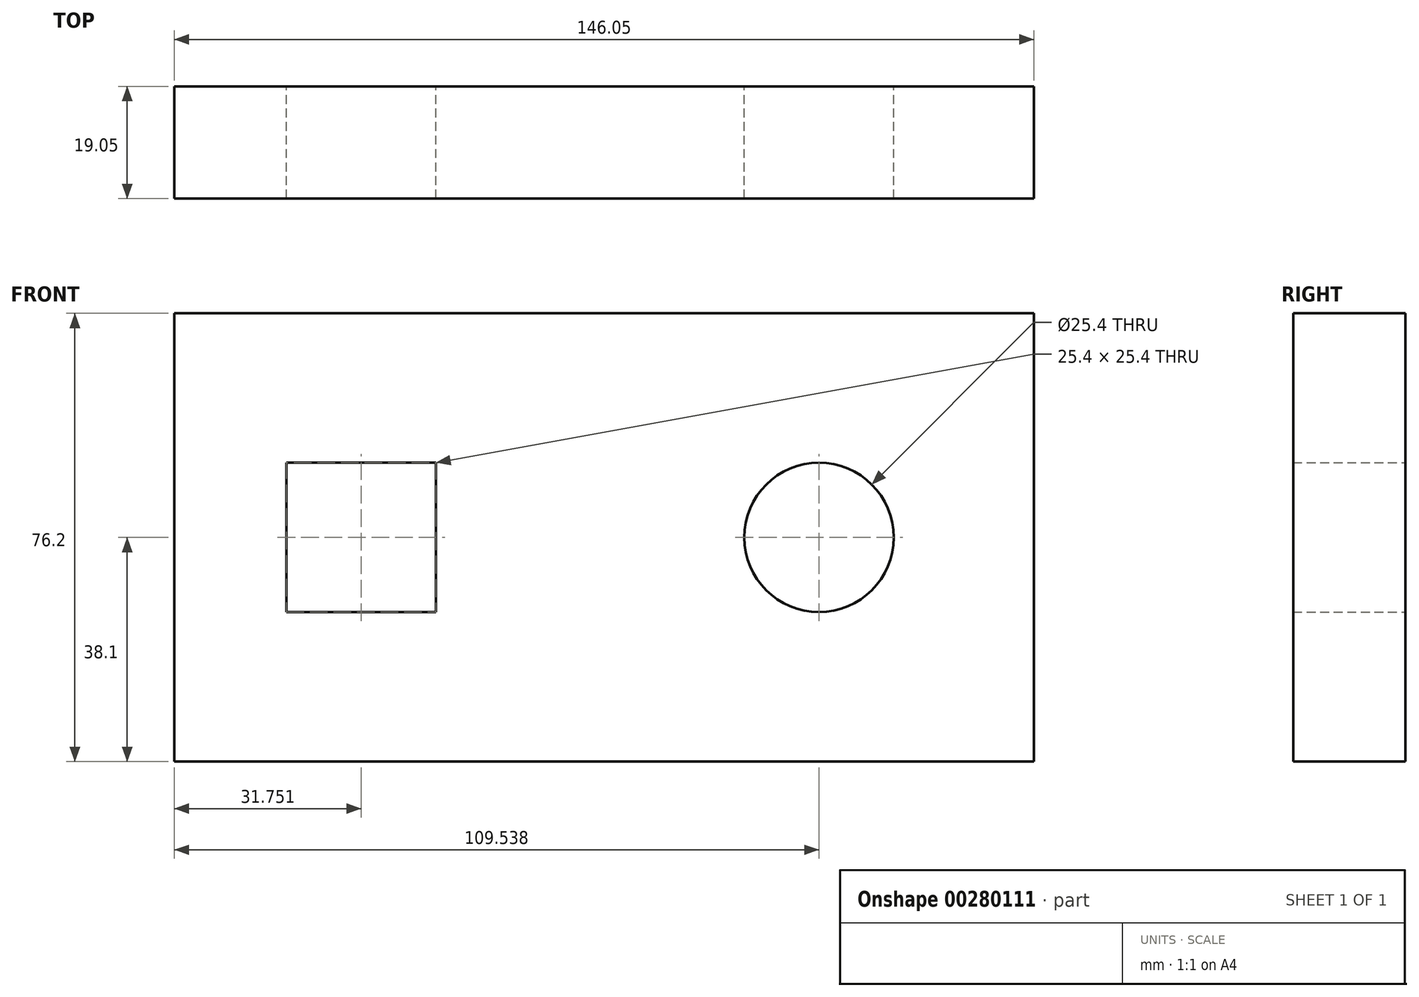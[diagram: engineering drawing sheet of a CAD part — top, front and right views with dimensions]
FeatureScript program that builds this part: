
annotation { "Feature Type Name" : "Feature", "Feature Type Description" : "" }
export const myFeature = defineFeature(function(context is Context, id is Id, definition is map)
    precondition{}
    {
        {
            var Q0;
            Q0=qCreatedBy(makeId("Front.planeOp"),FACE);
            var sketch = newSketch(context, id + "F0", { "sketchPlane" : qUnion([Q0])});
            skLineSegment(sketch, "E0.bottom", {"start": v(0, 0) * mm, "end": v(-146.05, 0) * mm});
            skLineSegment(sketch, "E0.top", {"start": v(0, 76.2) * mm, "end": v(-146.05, 76.2) * mm});
            skLineSegment(sketch, "E0.left", {"start": v(0, 0) * mm, "end": v(0, 76.2) * mm});
            skLineSegment(sketch, "E0.right", {"start": v(-146.05, 0) * mm, "end": v(-146.05, 76.2) * mm});
            skLineSegment(sketch, "E1.bottom", {"start": v(-127, 50.8) * mm, "end": v(-101.6, 50.8) * mm});
            skLineSegment(sketch, "E1.top", {"start": v(-127, 25.4) * mm, "end": v(-101.6, 25.4) * mm});
            skLineSegment(sketch, "E1.left", {"start": v(-127, 50.8) * mm, "end": v(-127, 25.4) * mm});
            skLineSegment(sketch, "E1.right", {"start": v(-101.6, 50.8) * mm, "end": v(-101.6, 25.4) * mm});
            skCircle(sketch, "E2", {"center": v(-36.51, 38.1) * mm, "radius": 12.7 * mm});
            skSolve(sketch);
        }
        {
            var Q0;
            Q0=makeQuery(id+"F0.imprint","IMPRINT",FACE,{"disambiguationData":[TD([[makeQuery(id+"F0.imprint","IMPRINT",EDGE,{"derivedFrom":sQuery(id+"F0.wireOp",EDGE,"E0.bottom")}),-1.0]])]});
            extrude(context, id + "F1", {"entities" : qUnion([Q0]), "depth" : 19.05 * mm});
        }
    });
